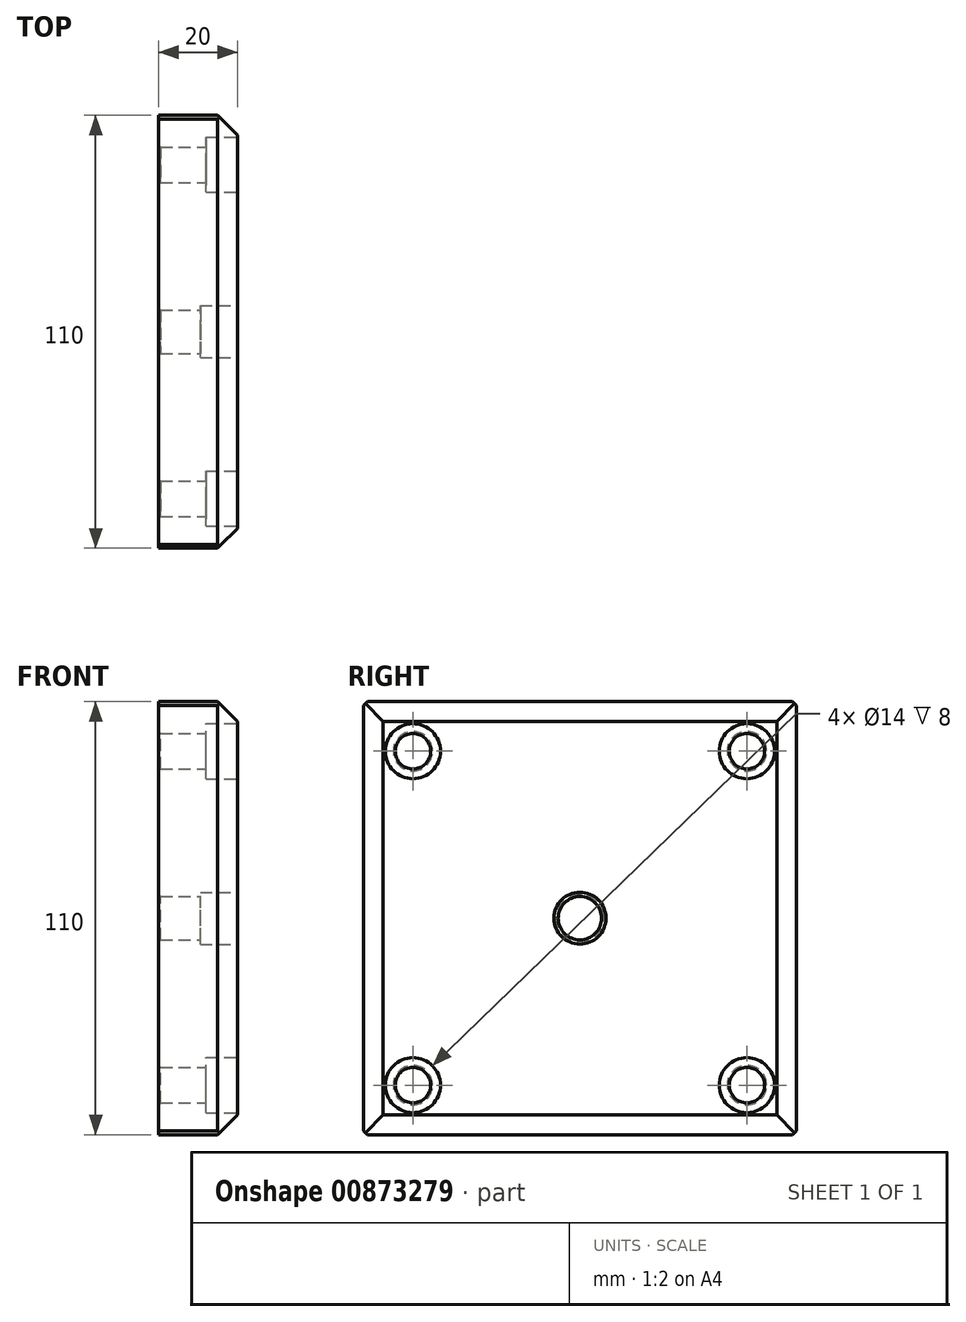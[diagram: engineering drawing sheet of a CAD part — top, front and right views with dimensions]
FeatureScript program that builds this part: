
annotation { "Feature Type Name" : "Feature", "Feature Type Description" : "" }
export const myFeature = defineFeature(function(context is Context, id is Id, definition is map)
    precondition{}
    {
        {
            var Q0;
            Q0=qCreatedBy(makeId("Right.planeOp"),FACE);
            var sketch = newSketch(context, id + "F0", { "sketchPlane" : qUnion([Q0])});
            skLineSegment(sketch, "E0.bottom", {"start": v(55, 55) * mm, "end": v(-55, 55) * mm});
            skLineSegment(sketch, "E0.top", {"start": v(55, -55) * mm, "end": v(-55, -55) * mm});
            skLineSegment(sketch, "E0.left", {"start": v(55, 55) * mm, "end": v(55, -55) * mm});
            skLineSegment(sketch, "E0.right", {"start": v(-55, 55) * mm, "end": v(-55, -55) * mm});
            skPoint(sketch, "E0.middle", {"position": v(0, 0) * mm});
            skCircle(sketch, "E1", {"center": v(0, 0) * mm, "radius": 60 * mm, "construction": true});
            skCircle(sketch, "E2", {"center": v(0, 0) * mm, "radius": 6.6 * mm});
            skCircle(sketch, "E3", {"center": v(0, 0) * mm, "radius": 5.5 * mm});
            skLineSegment(sketch, "E4", {"start": v(0, 0) * mm, "end": v(66.67, 66.67) * mm, "construction": true});
            skLineSegment(sketch, "E5", {"start": v(0, 0) * mm, "end": v(85.7, 0) * mm, "construction": true});
            skCircle(sketch, "E6", {"center": v(42.43, 42.43) * mm, "radius": 7 * mm});
            skCircle(sketch, "E7", {"center": v(42.43, 42.43) * mm, "radius": 4.5 * mm});
            skCircle(sketch, "E8.1.0", {"center": v(-42.43, 42.43) * mm, "radius": 4.5 * mm});
            skCircle(sketch, "E8.1.1", {"center": v(-42.43, 42.43) * mm, "radius": 7 * mm});
            skCircle(sketch, "E8.2.0", {"center": v(-42.43, -42.43) * mm, "radius": 4.5 * mm});
            skCircle(sketch, "E8.2.1", {"center": v(-42.43, -42.43) * mm, "radius": 7 * mm});
            skCircle(sketch, "E8.3.0", {"center": v(42.43, -42.43) * mm, "radius": 4.5 * mm});
            skCircle(sketch, "E8.3.1", {"center": v(42.43, -42.43) * mm, "radius": 7 * mm});
            skSolve(sketch);
        }
        {
            var Q0;
            Q0=makeQuery(id+"F0.imprint","IMPRINT",FACE,{"disambiguationData":[TD([[makeQuery(id+"F0.imprint","IMPRINT",EDGE,{"derivedFrom":sQuery(id+"F0.wireOp",EDGE,"E0.bottom")}),1.0]])]});
            var Q1;
            Q1=makeQuery(id+"F0.imprint","IMPRINT",FACE,{"disambiguationData":[TD([[makeQuery(id+"F0.imprint","IMPRINT",EDGE,{"derivedFrom":sQuery(id+"F0.wireOp",EDGE,"E8.1.0")}),1.0]])]});
            var Q2;
            Q2=makeQuery(id+"F0.imprint","IMPRINT",FACE,{"disambiguationData":[TD([[makeQuery(id+"F0.imprint","IMPRINT",EDGE,{"derivedFrom":sQuery(id+"F0.wireOp",EDGE,"E8.1.0")}),-1.0]])]});
            var Q3;
            Q3=makeQuery(id+"F0.imprint","IMPRINT",FACE,{"disambiguationData":[TD([[makeQuery(id+"F0.imprint","IMPRINT",EDGE,{"derivedFrom":sQuery(id+"F0.wireOp",EDGE,"E2")}),1.0]])]});
            var Q4;
            Q4=makeQuery(id+"F0.imprint","IMPRINT",FACE,{"disambiguationData":[TD([[makeQuery(id+"F0.imprint","IMPRINT",EDGE,{"derivedFrom":sQuery(id+"F0.wireOp",EDGE,"E3")}),1.0]])]});
            var Q5;
            Q5=makeQuery(id+"F0.imprint","IMPRINT",FACE,{"disambiguationData":[TD([[makeQuery(id+"F0.imprint","IMPRINT",EDGE,{"derivedFrom":sQuery(id+"F0.wireOp",EDGE,"E8.2.0")}),-1.0]])]});
            var Q6;
            Q6=makeQuery(id+"F0.imprint","IMPRINT",FACE,{"disambiguationData":[TD([[makeQuery(id+"F0.imprint","IMPRINT",EDGE,{"derivedFrom":sQuery(id+"F0.wireOp",EDGE,"E8.2.0")}),1.0]])]});
            var Q7;
            Q7=makeQuery(id+"F0.imprint","IMPRINT",FACE,{"disambiguationData":[TD([[makeQuery(id+"F0.imprint","IMPRINT",EDGE,{"derivedFrom":sQuery(id+"F0.wireOp",EDGE,"E8.3.0")}),-1.0]])]});
            var Q8;
            Q8=makeQuery(id+"F0.imprint","IMPRINT",FACE,{"disambiguationData":[TD([[makeQuery(id+"F0.imprint","IMPRINT",EDGE,{"derivedFrom":sQuery(id+"F0.wireOp",EDGE,"E8.3.0")}),1.0]])]});
            var Q9;
            Q9=makeQuery(id+"F0.imprint","IMPRINT",FACE,{"disambiguationData":[TD([[makeQuery(id+"F0.imprint","IMPRINT",EDGE,{"derivedFrom":sQuery(id+"F0.wireOp",EDGE,"E6")}),1.0]])]});
            var Q10;
            Q10=makeQuery(id+"F0.imprint","IMPRINT",FACE,{"disambiguationData":[TD([[makeQuery(id+"F0.imprint","IMPRINT",EDGE,{"derivedFrom":sQuery(id+"F0.wireOp",EDGE,"E7")}),1.0]])]});
            extrude(context, id + "F1", {"entities" : qUnion([Q0, Q1, Q2, Q3, Q4, Q5, Q6, Q7, Q8, Q9, Q10]), "oppositeDirection" : true, "depth" : 20 * mm, "offsetDistance" : 25 * mm});
        }
        {
            var Q0;
            Q0=makeQuery(id+"F0.imprint","IMPRINT",FACE,{"disambiguationData":[TD([[makeQuery(id+"F0.imprint","IMPRINT",EDGE,{"derivedFrom":sQuery(id+"F0.wireOp",EDGE,"E8.1.0")}),1.0]])]});
            var Q1;
            Q1=makeQuery(id+"F0.imprint","IMPRINT",FACE,{"disambiguationData":[TD([[makeQuery(id+"F0.imprint","IMPRINT",EDGE,{"derivedFrom":sQuery(id+"F0.wireOp",EDGE,"E8.3.0")}),1.0]])]});
            var Q2;
            Q2=makeQuery(id+"F0.imprint","IMPRINT",FACE,{"disambiguationData":[TD([[makeQuery(id+"F0.imprint","IMPRINT",EDGE,{"derivedFrom":sQuery(id+"F0.wireOp",EDGE,"E8.2.0")}),1.0]])]});
            var Q3;
            Q3=makeQuery(id+"F0.imprint","IMPRINT",FACE,{"disambiguationData":[TD([[makeQuery(id+"F0.imprint","IMPRINT",EDGE,{"derivedFrom":sQuery(id+"F0.wireOp",EDGE,"E3")}),1.0]])]});
            var Q4;
            Q4=makeQuery(id+"F0.imprint","IMPRINT",FACE,{"disambiguationData":[TD([[makeQuery(id+"F0.imprint","IMPRINT",EDGE,{"derivedFrom":sQuery(id+"F0.wireOp",EDGE,"E7")}),1.0]])]});
            extrude(context, id + "F2", {"entities" : qUnion([Q0, Q1, Q2, Q3, Q4]), "operationType" : NewBodyOperationType.REMOVE, "endBound" : BoundingType.THROUGH_ALL, "oppositeDirection" : true, "depth" : 25 * mm, "offsetDistance" : 25 * mm});
        }
        {
            var Q0;
            Q0=makeQuery(id+"F0.imprint","IMPRINT",FACE,{"disambiguationData":[TD([[makeQuery(id+"F0.imprint","IMPRINT",EDGE,{"derivedFrom":sQuery(id+"F0.wireOp",EDGE,"E8.1.0")}),-1.0]])]});
            var Q1;
            Q1=makeQuery(id+"F0.imprint","IMPRINT",FACE,{"disambiguationData":[TD([[makeQuery(id+"F0.imprint","IMPRINT",EDGE,{"derivedFrom":sQuery(id+"F0.wireOp",EDGE,"E6")}),1.0]])]});
            var Q2;
            Q2=makeQuery(id+"F0.imprint","IMPRINT",FACE,{"disambiguationData":[TD([[makeQuery(id+"F0.imprint","IMPRINT",EDGE,{"derivedFrom":sQuery(id+"F0.wireOp",EDGE,"E8.2.0")}),-1.0]])]});
            var Q3;
            Q3=makeQuery(id+"F0.imprint","IMPRINT",FACE,{"disambiguationData":[TD([[makeQuery(id+"F0.imprint","IMPRINT",EDGE,{"derivedFrom":sQuery(id+"F0.wireOp",EDGE,"E8.3.0")}),-1.0]])]});
            extrude(context, id + "F3", {"entities" : qUnion([Q0, Q1, Q2, Q3]), "operationType" : NewBodyOperationType.REMOVE, "oppositeDirection" : true, "depth" : 8 * mm, "offsetDistance" : 25 * mm});
        }
        {
            var Q0;
            Q0=makeQuery(id+"F0.imprint","IMPRINT",FACE,{"disambiguationData":[TD([[makeQuery(id+"F0.imprint","IMPRINT",EDGE,{"derivedFrom":sQuery(id+"F0.wireOp",EDGE,"E2")}),1.0]])]});
            extrude(context, id + "F4", {"entities" : qUnion([Q0]), "operationType" : NewBodyOperationType.REMOVE, "oppositeDirection" : true, "depth" : 9.4 * mm, "offsetDistance" : 25 * mm});
        }
        {
            var Q0;
            Q0=makeQuery(id+"F3.boolean.opBoolean","COPY",EDGE,{"derivedFrom":makeQuery(id+"F3.opExtrude","CAP_EDGE",EDGE,{"disambiguationData":[OSD([sQuery(id+"F0.wireOp",EDGE,"E8.1.1")])],"isStart":true})});
            var Q1;
            Q1=makeQuery(id+"F3.boolean.opBoolean","COPY",EDGE,{"derivedFrom":makeQuery(id+"F3.opExtrude","CAP_EDGE",EDGE,{"disambiguationData":[OSD([sQuery(id+"F0.wireOp",EDGE,"E6")])],"isStart":true})});
            var Q2;
            Q2=makeQuery(id+"F3.boolean.opBoolean","COPY",EDGE,{"derivedFrom":makeQuery(id+"F3.opExtrude","CAP_EDGE",EDGE,{"disambiguationData":[OSD([sQuery(id+"F0.wireOp",EDGE,"E8.2.1")])],"isStart":true})});
            var Q3;
            Q3=makeQuery(id+"F3.boolean.opBoolean","COPY",EDGE,{"derivedFrom":makeQuery(id+"F3.opExtrude","CAP_EDGE",EDGE,{"disambiguationData":[OSD([sQuery(id+"F0.wireOp",EDGE,"E8.3.1")])],"isStart":true})});
            var Q4;
            Q4=makeQuery(id+"F1.opExtrude","SWEPT_EDGE",EDGE,{"disambiguationData":[OSD([sQuery(id+"F0.wireOp",EDGE,"E0.top"),sQuery(id+"F0.wireOp",EDGE,"E0.left")])]});
            var Q5;
            Q5=makeQuery(id+"F1.opExtrude","SWEPT_EDGE",EDGE,{"disambiguationData":[OSD([sQuery(id+"F0.wireOp",EDGE,"E0.bottom"),sQuery(id+"F0.wireOp",EDGE,"E0.left")])]});
            var Q6;
            Q6=makeQuery(id+"F1.opExtrude","SWEPT_EDGE",EDGE,{"disambiguationData":[OSD([sQuery(id+"F0.wireOp",EDGE,"E0.bottom"),sQuery(id+"F0.wireOp",EDGE,"E0.right")])]});
            var Q7;
            Q7=makeQuery(id+"F1.opExtrude","SWEPT_EDGE",EDGE,{"disambiguationData":[OSD([sQuery(id+"F0.wireOp",EDGE,"E0.top"),sQuery(id+"F0.wireOp",EDGE,"E0.right")])]});
            chamfer(context, id + "F5", {"entities" : qUnion([Q0, Q1, Q2, Q3, Q4, Q5, Q6, Q7]), "width" : 1 * mm, "tangentPropagation" : true});
        }
        {
            var Q0;
            Q0=makeQuery(id+"F1.opExtrude","CAP_EDGE",EDGE,{"disambiguationData":[OSD([sQuery(id+"F0.wireOp",EDGE,"E0.right")])],"isStart":true});
            var Q1;
            Q1=makeQuery(id+"F1.opExtrude","CAP_EDGE",EDGE,{"disambiguationData":[OSD([sQuery(id+"F0.wireOp",EDGE,"E0.bottom")])],"isStart":true});
            var Q2;
            Q2=makeQuery(id+"F1.opExtrude","CAP_EDGE",EDGE,{"disambiguationData":[OSD([sQuery(id+"F0.wireOp",EDGE,"E0.top")])],"isStart":true});
            var Q3;
            Q3=makeQuery(id+"F1.opExtrude","CAP_EDGE",EDGE,{"disambiguationData":[OSD([sQuery(id+"F0.wireOp",EDGE,"E0.left")])],"isStart":true});
            chamfer(context, id + "F6", {"entities" : qUnion([Q0, Q1, Q2, Q3]), "width" : 5 * mm, "tangentPropagation" : true});
        }
        {
            var Q0;
            Q0=makeQuery(id+"F2.boolean.opBoolean","INTERSECT",EDGE,{"derivedFrom":[makeQuery(id+"F1.opExtrude","CAP_FACE",FACE,{"disambiguationData":[OSD([sQuery(id+"F0.wireOp",EDGE,"E0.bottom"),sQuery(id+"F0.wireOp",EDGE,"E0.top"),sQuery(id+"F0.wireOp",EDGE,"E0.left"),sQuery(id+"F0.wireOp",EDGE,"E0.right")])],"isStart":false}),makeQuery(id+"F2.opExtrude","SWEPT_FACE",FACE,{"disambiguationData":[OSD([sQuery(id+"F0.wireOp",EDGE,"E8.3.0")])]})]});
            var Q1;
            Q1=makeQuery(id+"F2.boolean.opBoolean","INTERSECT",EDGE,{"derivedFrom":[makeQuery(id+"F1.opExtrude","CAP_FACE",FACE,{"disambiguationData":[OSD([sQuery(id+"F0.wireOp",EDGE,"E0.bottom"),sQuery(id+"F0.wireOp",EDGE,"E0.top"),sQuery(id+"F0.wireOp",EDGE,"E0.left"),sQuery(id+"F0.wireOp",EDGE,"E0.right")])],"isStart":false}),makeQuery(id+"F2.opExtrude","SWEPT_FACE",FACE,{"disambiguationData":[OSD([sQuery(id+"F0.wireOp",EDGE,"E7")])]})]});
            var Q2;
            Q2=makeQuery(id+"F2.boolean.opBoolean","INTERSECT",EDGE,{"derivedFrom":[makeQuery(id+"F1.opExtrude","CAP_FACE",FACE,{"disambiguationData":[OSD([sQuery(id+"F0.wireOp",EDGE,"E0.bottom"),sQuery(id+"F0.wireOp",EDGE,"E0.top"),sQuery(id+"F0.wireOp",EDGE,"E0.left"),sQuery(id+"F0.wireOp",EDGE,"E0.right")])],"isStart":false}),makeQuery(id+"F2.opExtrude","SWEPT_FACE",FACE,{"disambiguationData":[OSD([sQuery(id+"F0.wireOp",EDGE,"E8.1.0")])]})]});
            var Q3;
            Q3=makeQuery(id+"F2.boolean.opBoolean","INTERSECT",EDGE,{"derivedFrom":[makeQuery(id+"F1.opExtrude","CAP_FACE",FACE,{"disambiguationData":[OSD([sQuery(id+"F0.wireOp",EDGE,"E0.bottom"),sQuery(id+"F0.wireOp",EDGE,"E0.top"),sQuery(id+"F0.wireOp",EDGE,"E0.left"),sQuery(id+"F0.wireOp",EDGE,"E0.right")])],"isStart":false}),makeQuery(id+"F2.opExtrude","SWEPT_FACE",FACE,{"disambiguationData":[OSD([sQuery(id+"F0.wireOp",EDGE,"E8.2.0")])]})]});
            var Q4;
            Q4=makeQuery(id+"F2.boolean.opBoolean","INTERSECT",EDGE,{"derivedFrom":[makeQuery(id+"F1.opExtrude","CAP_FACE",FACE,{"disambiguationData":[OSD([sQuery(id+"F0.wireOp",EDGE,"E0.bottom"),sQuery(id+"F0.wireOp",EDGE,"E0.top"),sQuery(id+"F0.wireOp",EDGE,"E0.left"),sQuery(id+"F0.wireOp",EDGE,"E0.right")])],"isStart":false}),makeQuery(id+"F2.opExtrude","SWEPT_FACE",FACE,{"disambiguationData":[OSD([sQuery(id+"F0.wireOp",EDGE,"E3")])]})]});
            chamfer(context, id + "F7", {"entities" : qUnion([Q0, Q1, Q2, Q3, Q4]), "width" : 0.5 * mm, "tangentPropagation" : true});
        }
    });
